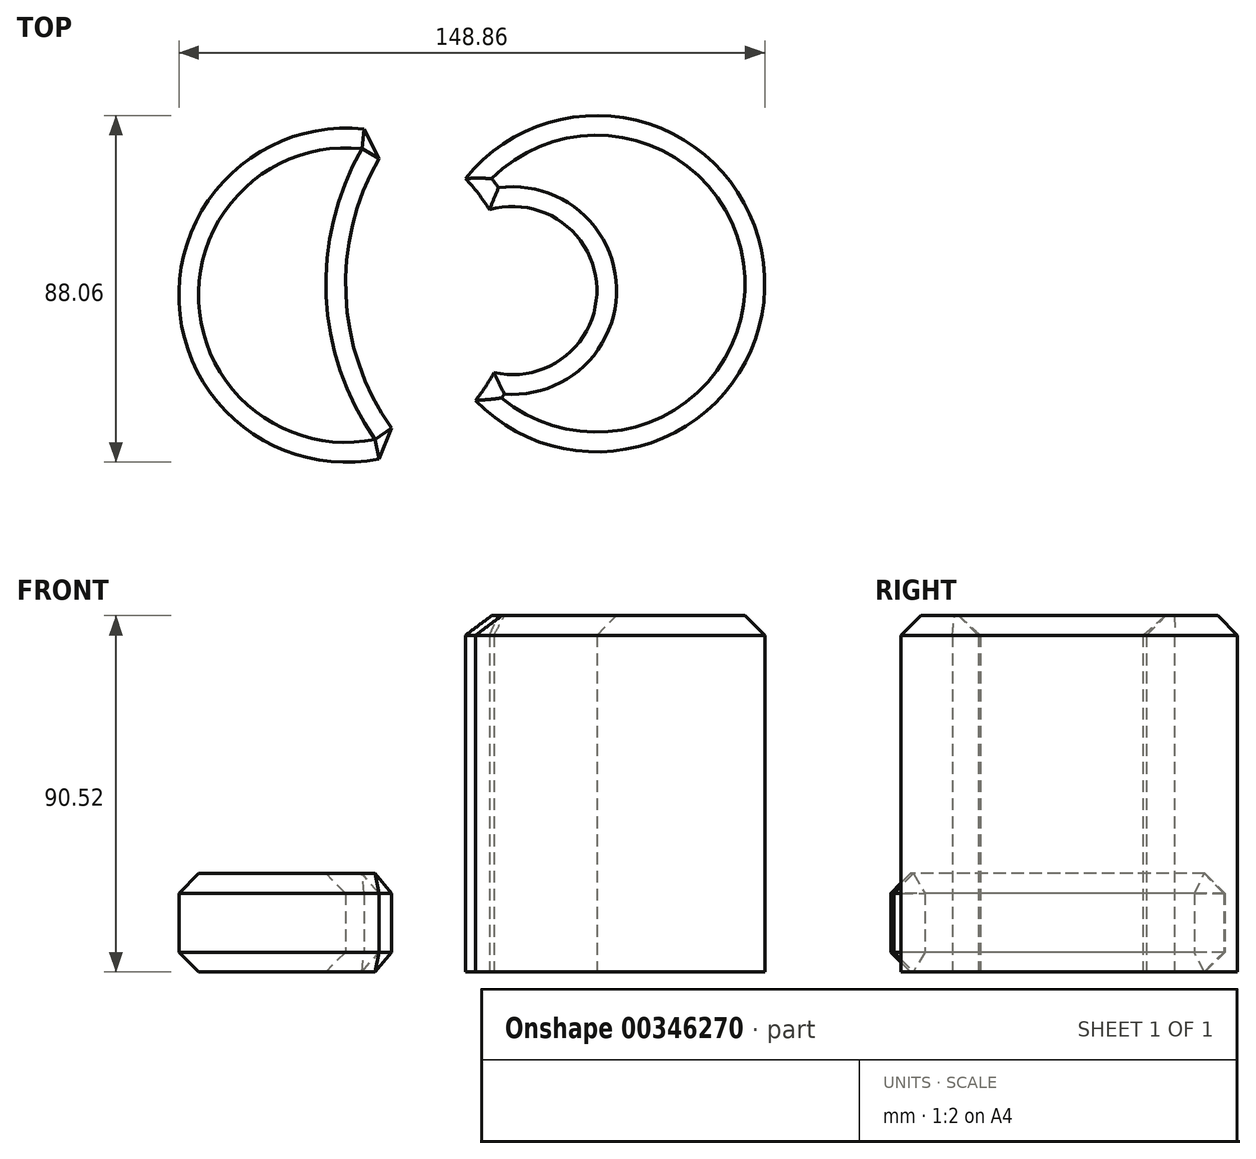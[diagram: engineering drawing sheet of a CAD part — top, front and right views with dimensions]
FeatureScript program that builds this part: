
annotation { "Feature Type Name" : "Feature", "Feature Type Description" : "" }
export const myFeature = defineFeature(function(context is Context, id is Id, definition is map)
    precondition{}
    {
        {
            var Q0;
            Q0=qCreatedBy(makeId("Top.planeOp"),FACE);
            var sketch = newSketch(context, id + "F0", { "sketchPlane" : qUnion([Q0])});
            skCircle(sketch, "E0", {"center": v(0, 0) * mm, "radius": 42.43 * mm});
            skCircle(sketch, "E1", {"center": v(42.41, 1.17) * mm, "radius": 21.36 * mm});
            skCircle(sketch, "E2", {"center": v(63.7, 2.91) * mm, "radius": 63.77 * mm});
            skCircle(sketch, "E3", {"center": v(63.7, 2.91) * mm, "radius": 42.72 * mm});
            skSolve(sketch);
        }
        {
            var Q0;
            Q0 = qSketchRegion(id + "F0", true);
            var sketch = newSketch(context, id + "F1", { "sketchPlane" : qUnion([Q0])});
            skSolve(sketch);
        }
        {
            var Q0;
            {var subQ0=sQuery(id+"F0.wireOp",EDGE,"E3");var subQ1=sQuery(id+"F0.wireOp",EDGE,"E0");var subQ2=makeQuery(id+"F0.imprint","INTERSECT",VERTEX,{"disambiguationData":[OD(0.0)],"derivedFrom":[subQ1,subQ0]});Q0=makeQuery(id+"F0.imprint","IMPRINT",FACE,{"disambiguationData":[TD([[makeQuery(id+"F0.imprint","IMPRINT",EDGE,{"disambiguationData":[TD([[subQ2,1.0]])],"derivedFrom":subQ1}),-1.0]])]});}
            extrude(context, id + "F2", {"entities" : qUnion([Q0]), "depth" : 90.52 * mm});
        }
        {
            var Q0;
            {var subQ0=sQuery(id+"F0.wireOp",EDGE,"E2");var subQ1=sQuery(id+"F0.wireOp",EDGE,"E0");var subQ2=makeQuery(id+"F0.imprint","INTERSECT",VERTEX,{"disambiguationData":[OD(0.0)],"derivedFrom":[subQ1,subQ0]});Q0=makeQuery(id+"F1.imprint","IMPRINT",FACE,{"disambiguationData":[TD([[makeQuery(id+"F1.imprint","IMPRINT",EDGE,{"derivedFrom":makeQuery(id+"F0.imprint","IMPRINT",EDGE,{"disambiguationData":[TD([[subQ2,-1.0]])],"derivedFrom":subQ1})}),1.0]])]});}
            var Q1;
            {var subQ0=sQuery(id+"F0.wireOp",EDGE,"E2");var subQ1=sQuery(id+"F0.wireOp",EDGE,"E0");var subQ2=makeQuery(id+"F0.imprint","INTERSECT",VERTEX,{"disambiguationData":[OD(0.0)],"derivedFrom":[subQ1,subQ0]});Q1=makeQuery(id+"F1.imprint","IMPRINT",FACE,{"disambiguationData":[TD([[makeQuery(id+"F1.imprint","IMPRINT",EDGE,{"derivedFrom":makeQuery(id+"F0.imprint","IMPRINT",EDGE,{"disambiguationData":[TD([[subQ2,1.0]])],"derivedFrom":subQ1})}),-1.0]])]});}
            extrude(context, id + "F3", {"entities" : qUnion([Q0, Q1]), "operationType" : NewBodyOperationType.ADD, "depth" : 25 * mm});
        }
        {
            var Q0;
            {var subQ0=sQuery(id+"F0.wireOp",EDGE,"E2");var subQ1=sQuery(id+"F0.wireOp",EDGE,"E0");Q0=makeQuery(id+"F3.opExtrude","SWEPT_FACE",FACE,{"disambiguationData":[OSD([subQ0]),TDD([makeQuery(id+"F1.imprint","IMPRINT",EDGE,{"derivedFrom":makeQuery(id+"F0.imprint","IMPRINT",EDGE,{"disambiguationData":[TD([[makeQuery(id+"F0.imprint","INTERSECT",VERTEX,{"disambiguationData":[OD(0.0)],"derivedFrom":[subQ1,subQ0]}),1.0]])],"derivedFrom":subQ0})})])]});}
            var Q1;
            Q1=makeQuery(id+"F3.opExtrude","CAP_FACE",FACE,{"disambiguationData":[OSD([sQuery(id+"F0.wireOp",EDGE,"E0"),sQuery(id+"F0.wireOp",EDGE,"E2")])],"isStart":false});
            var Q2;
            {var subQ0=sQuery(id+"F0.wireOp",EDGE,"E2");var subQ1=sQuery(id+"F0.wireOp",EDGE,"E0");Q2=makeQuery(id+"F3.opExtrude","CAP_EDGE",EDGE,{"disambiguationData":[OSD([subQ1]),TDD([makeQuery(id+"F1.imprint","IMPRINT",EDGE,{"derivedFrom":makeQuery(id+"F0.imprint","IMPRINT",EDGE,{"disambiguationData":[TD([[makeQuery(id+"F0.imprint","INTERSECT",VERTEX,{"disambiguationData":[OD(0.0)],"derivedFrom":[subQ1,subQ0]}),-1.0]])],"derivedFrom":subQ1})})])],"isStart":true});}
            var Q3;
            Q3=makeQuery(id+"F2.opExtrude","CAP_EDGE",EDGE,{"disambiguationData":[OSD([sQuery(id+"F0.wireOp",EDGE,"E3")])],"isStart":false});
            var Q4;
            {var subQ0=sQuery(id+"F0.wireOp",EDGE,"E0");Q4=makeQuery(id+"F2.opExtrude","CAP_EDGE",EDGE,{"disambiguationData":[OSD([subQ0]),TDD([makeQuery(id+"F0.imprint","IMPRINT",EDGE,{"disambiguationData":[TD([[makeQuery(id+"F0.imprint","INTERSECT",VERTEX,{"disambiguationData":[OD(0.0)],"derivedFrom":[subQ0,sQuery(id+"F0.wireOp",EDGE,"E3")]}),1.0]])],"derivedFrom":subQ0})])],"isStart":false});}
            var Q5;
            Q5=makeQuery(id+"F2.opExtrude","CAP_EDGE",EDGE,{"disambiguationData":[OSD([sQuery(id+"F0.wireOp",EDGE,"E1")])],"isStart":false});
            var Q6;
            {var subQ0=sQuery(id+"F0.wireOp",EDGE,"E0");Q6=makeQuery(id+"F2.opExtrude","CAP_EDGE",EDGE,{"disambiguationData":[OSD([subQ0]),TDD([makeQuery(id+"F0.imprint","IMPRINT",EDGE,{"disambiguationData":[TD([[makeQuery(id+"F0.imprint","INTERSECT",VERTEX,{"disambiguationData":[OD(1.0)],"derivedFrom":[subQ0,sQuery(id+"F0.wireOp",EDGE,"E3")]}),-1.0]])],"derivedFrom":subQ0})])],"isStart":false});}
            chamfer(context, id + "F4", {"entities" : qUnion([Q0, Q1, Q2, Q3, Q4, Q5, Q6]), "width" : 5 * mm, "tangentPropagation" : true});
        }
    });
